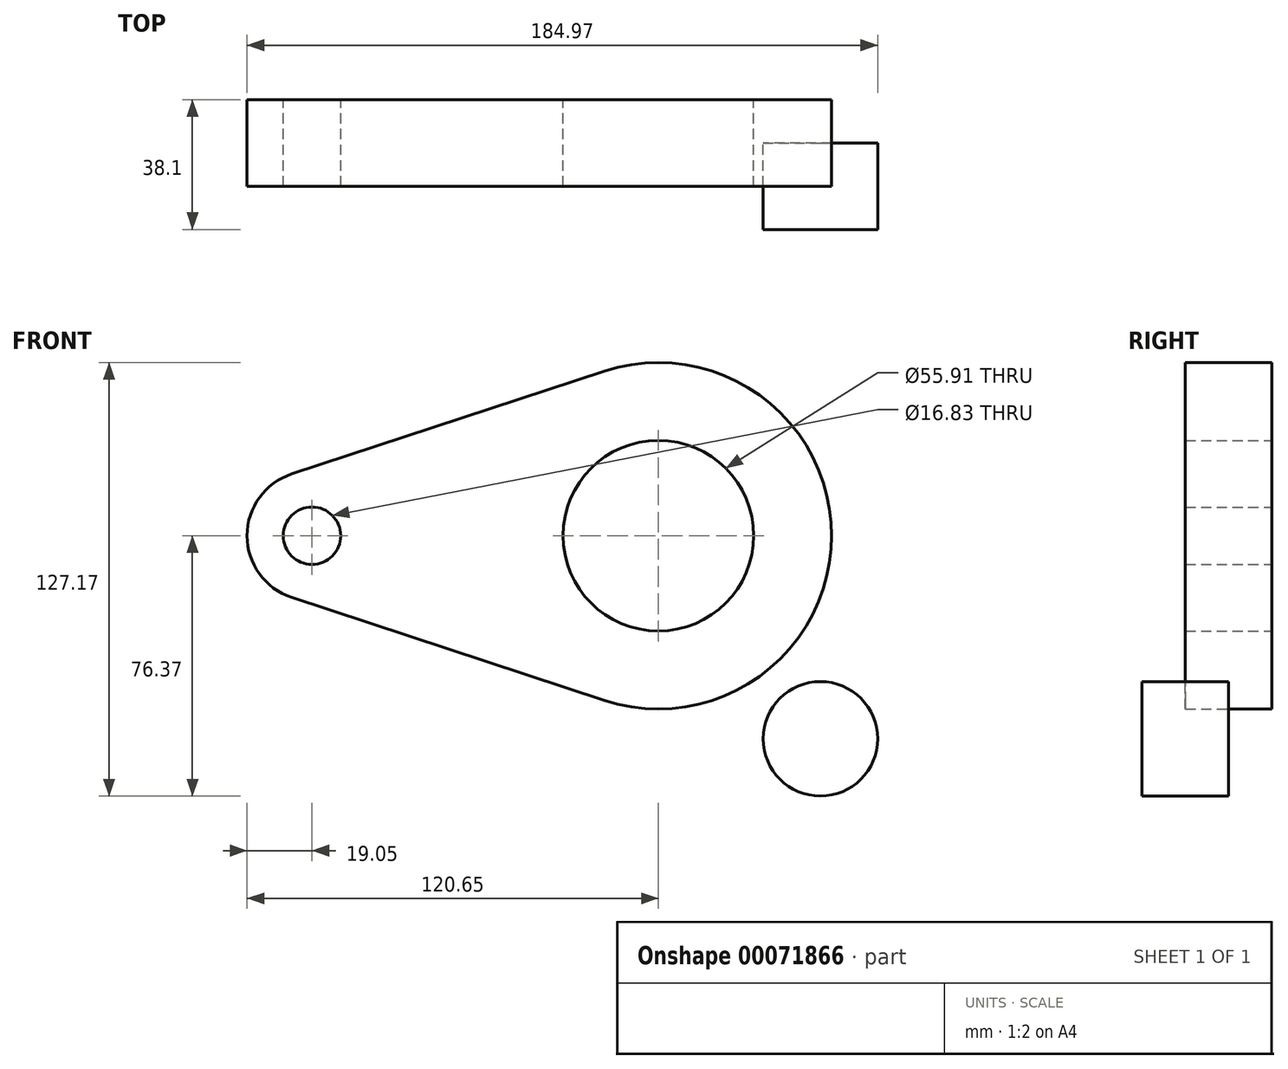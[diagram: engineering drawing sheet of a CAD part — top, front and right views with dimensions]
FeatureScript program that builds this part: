
annotation { "Feature Type Name" : "Feature", "Feature Type Description" : "" }
export const myFeature = defineFeature(function(context is Context, id is Id, definition is map)
    precondition{}
    {
        {
            var Q0;
            Q0=qCreatedBy(makeId("Front.planeOp"),FACE);
            var sketch = newSketch(context, id + "F0", { "sketchPlane" : qUnion([Q0])});
            skCircle(sketch, "E0", {"center": v(0, 0) * mm, "radius": 50.8 * mm});
            skCircle(sketch, "E1", {"center": v(-101.6, 0) * mm, "radius": 19.05 * mm});
            skLineSegment(sketch, "E2", {"start": v(-107.55, 18.1) * mm, "end": v(-15.88, 48.26) * mm});
            skLineSegment(sketch, "E3", {"start": v(-107.55, -18.1) * mm, "end": v(-15.87, -48.26) * mm});
            skCircle(sketch, "E4", {"center": v(0, 0) * mm, "radius": 27.95 * mm});
            skCircle(sketch, "E5", {"center": v(-101.6, 0) * mm, "radius": 8.42 * mm});
            skSolve(sketch);
        }
        {
            var Q0;
            Q0=qCreatedBy(makeId("Front.planeOp"),FACE);
            var sketch = newSketch(context, id + "F1", { "sketchPlane" : qUnion([Q0])});
            skCircle(sketch, "E6", {"center": v(47.53, -59.58) * mm, "radius": 16.8 * mm});
            skSolve(sketch);
        }
        {
            var Q0;
            Q0 = qSketchRegion(id + "F1", true);
            extrude(context, id + "F2", {"entities" : qUnion([Q0]), "depth" : 25.4 * mm});
        }
        {
            var Q0;
            Q0 = qSketchRegion(id + "F0", true);
            extrude(context, id + "F3", {"entities" : qUnion([Q0]), "endBound" : BoundingType.SYMMETRIC, "depth" : 25.4 * mm});
        }
    });
